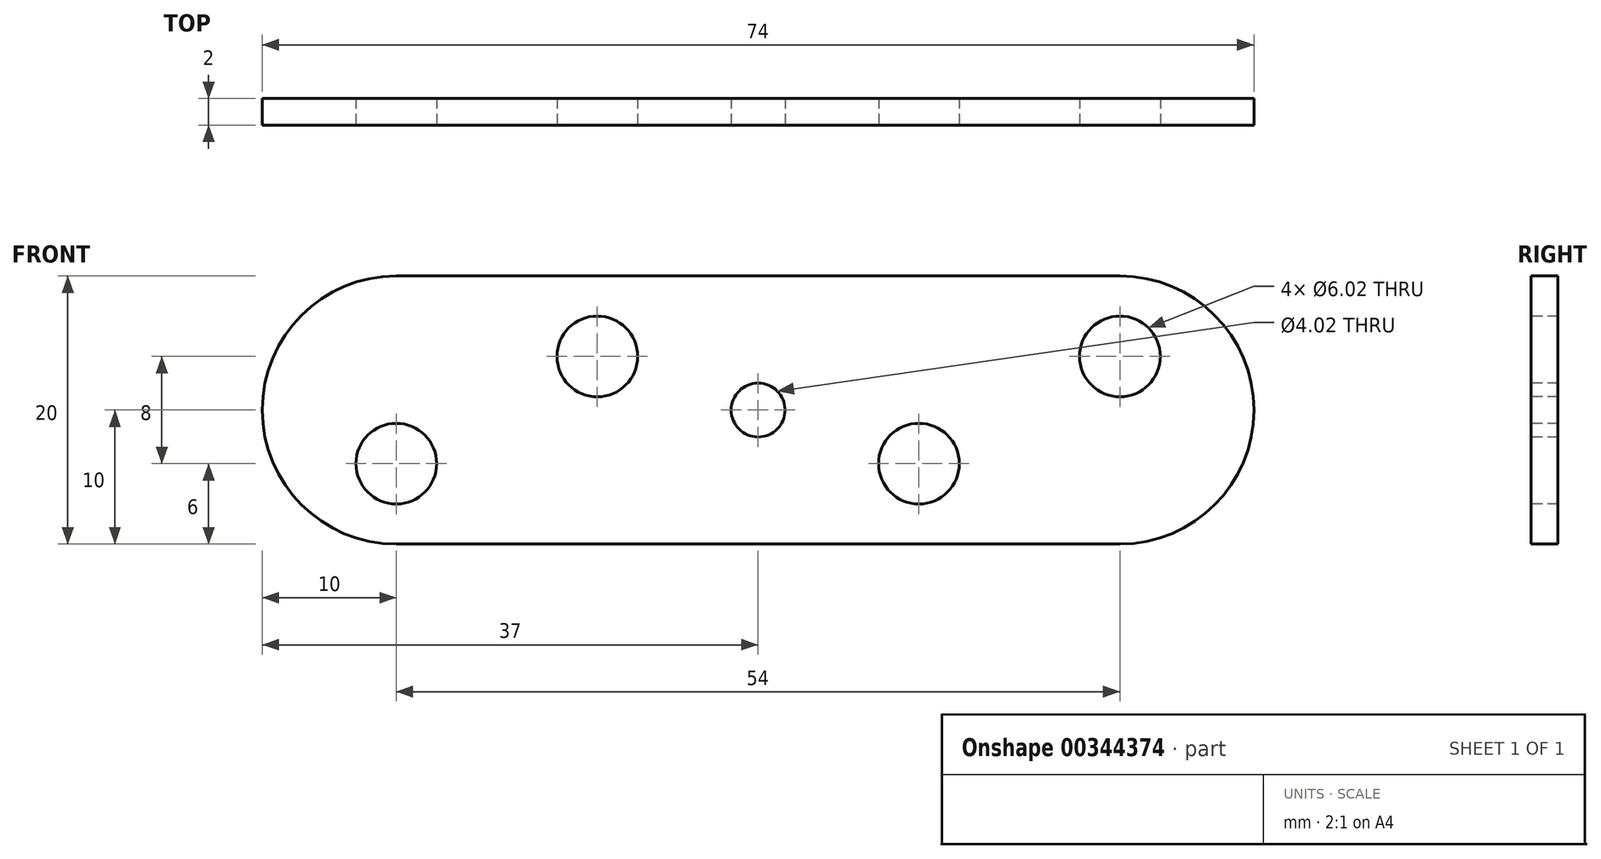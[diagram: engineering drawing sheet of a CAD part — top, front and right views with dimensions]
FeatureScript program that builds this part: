
annotation { "Feature Type Name" : "Feature", "Feature Type Description" : "" }
export const myFeature = defineFeature(function(context is Context, id is Id, definition is map)
    precondition{}
    {
        {
            var Q0;
            Q0=qCreatedBy(makeId("Front.planeOp"),FACE);
            var sketch = newSketch(context, id + "F0", { "sketchPlane" : qUnion([Q0])});
            skLineSegment(sketch, "E0.bottom", {"start": v(27, 10) * mm, "end": v(-27, 10) * mm});
            skLineSegment(sketch, "E0.top", {"start": v(27, -10) * mm, "end": v(-27, -10) * mm});
            skLineSegment(sketch, "E0.left", {"start": v(37, 0) * mm, "end": v(37, 0) * mm});
            skLineSegment(sketch, "E0.right", {"start": v(-37, 0) * mm, "end": v(-37, 0) * mm});
            skPoint(sketch, "E0.middle", {"position": v(0, 0) * mm});
            skPoint(sketch, "E1.visualSharp", {"position": v(37, 10) * mm});
            skArc(sketch, "E1.filletArc", {"start": v(37, 0) * mm, "mid": v(34.07, 7.07) * mm, "end": v(27, 10) * mm});
            skPoint(sketch, "E2.visualSharp", {"position": v(37, -10) * mm});
            skArc(sketch, "E2.filletArc", {"start": v(27, -10) * mm, "mid": v(34.07, -7.07) * mm, "end": v(37, 0) * mm});
            skPoint(sketch, "E3.visualSharp", {"position": v(-37, 10) * mm});
            skArc(sketch, "E3.filletArc", {"start": v(-27, 10) * mm, "mid": v(-34.07, 7.07) * mm, "end": v(-37, 0) * mm});
            skPoint(sketch, "E4.visualSharp", {"position": v(-37, -10) * mm});
            skArc(sketch, "E4.filletArc", {"start": v(-37, 0) * mm, "mid": v(-34.07, -7.07) * mm, "end": v(-27, -10) * mm});
            skSolve(sketch);
        }
        {
            var Q0;
            Q0=makeQuery(id+"F0.imprint","IMPRINT",FACE,{"disambiguationData":[TD([[makeQuery(id+"F0.imprint","IMPRINT",EDGE,{"derivedFrom":sQuery(id+"F0.wireOp",EDGE,"E0.bottom")}),1.0]])]});
            extrude(context, id + "F1", {"entities" : qUnion([Q0]), "depth" : 2 * mm});
        }
        {
            var Q0;
            Q0=makeQuery(id+"F1.opExtrude","CAP_FACE",FACE,{"disambiguationData":[OSD([sQuery(id+"F0.wireOp",EDGE,"E0.bottom"),sQuery(id+"F0.wireOp",EDGE,"E0.top"),sQuery(id+"F0.wireOp",EDGE,"E1.filletArc"),sQuery(id+"F0.wireOp",EDGE,"E2.filletArc"),sQuery(id+"F0.wireOp",EDGE,"E3.filletArc"),sQuery(id+"F0.wireOp",EDGE,"E4.filletArc")])],"isStart":false});
            var sketch = newSketch(context, id + "F2", { "sketchPlane" : qUnion([Q0])});
            skLineSegment(sketch, "E5", {"start": v(-12, 4) * mm, "end": v(27, 4) * mm, "construction": true});
            skLineSegment(sketch, "E6", {"start": v(-27, -4) * mm, "end": v(12, -4) * mm, "construction": true});
            skSolve(sketch);
        }
        {
            var Q0;
            Q0=sQuery(id+"F2.wireOp",VERTEX,"E5.start");
            var Q1;
            Q1=sQuery(id+"F2.wireOp",VERTEX,"E6.start");
            var Q2;
            Q2=sQuery(id+"F2.wireOp",VERTEX,"E5.end");
            var Q3;
            Q3=sQuery(id+"F2.wireOp",VERTEX,"E6.end");
            var Q4;
            Q4=makeQuery(id+"F1.opExtrude","SWEPT_BODY",BODY,{"disambiguationData":[OSD([sQuery(id+"F0.wireOp",EDGE,"E0.bottom"),sQuery(id+"F0.wireOp",EDGE,"E0.top"),sQuery(id+"F0.wireOp",EDGE,"E1.filletArc"),sQuery(id+"F0.wireOp",EDGE,"E2.filletArc"),sQuery(id+"F0.wireOp",EDGE,"E3.filletArc"),sQuery(id+"F0.wireOp",EDGE,"E4.filletArc")])]});
            hole(context, id + "F3", {"style" : HoleStyle.SIMPLE, "endStyle" : HoleEndStyle.THROUGH, "holeDiameter" : 6.02 * mm, "isTappedThrough" : true, "tappedDepth" : 12 * mm, "tapClearance" : 3, "locations" : qUnion([Q0, Q1, Q2, Q3]), "scope" : qUnion([Q4])});
        }
        {
            var Q0;
            Q0=makeQuery(id+"F1.opExtrude","CAP_FACE",FACE,{"disambiguationData":[OSD([sQuery(id+"F0.wireOp",EDGE,"E0.bottom"),sQuery(id+"F0.wireOp",EDGE,"E0.top"),sQuery(id+"F0.wireOp",EDGE,"E1.filletArc"),sQuery(id+"F0.wireOp",EDGE,"E2.filletArc"),sQuery(id+"F0.wireOp",EDGE,"E3.filletArc"),sQuery(id+"F0.wireOp",EDGE,"E4.filletArc")])],"isStart":false});
            var sketch = newSketch(context, id + "F4", { "sketchPlane" : qUnion([Q0])});
            skPoint(sketch, "E7", {"position": v(0, 0) * mm});
            skSolve(sketch);
        }
        {
            var Q0;
            Q0=sQuery(id+"F4.wireOp",VERTEX,"E7");
            var Q1;
            Q1=makeQuery(id+"F1.opExtrude","SWEPT_BODY",BODY,{"disambiguationData":[OSD([sQuery(id+"F0.wireOp",EDGE,"E0.bottom"),sQuery(id+"F0.wireOp",EDGE,"E0.top"),sQuery(id+"F0.wireOp",EDGE,"E1.filletArc"),sQuery(id+"F0.wireOp",EDGE,"E2.filletArc"),sQuery(id+"F0.wireOp",EDGE,"E3.filletArc"),sQuery(id+"F0.wireOp",EDGE,"E4.filletArc")])]});
            hole(context, id + "F5", {"style" : HoleStyle.SIMPLE, "endStyle" : HoleEndStyle.THROUGH, "holeDiameter" : 4.02 * mm, "isTappedThrough" : true, "tappedDepth" : 12 * mm, "tapClearance" : 3, "locations" : qUnion([Q0]), "scope" : qUnion([Q1])});
        }
    });
